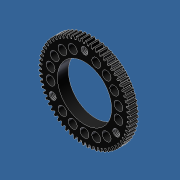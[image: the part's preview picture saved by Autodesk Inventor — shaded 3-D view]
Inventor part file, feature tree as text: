
AUTODESK INVENTOR PART (.ipt)
format: ipt  version: unknown  size: 705,536 bytes
history: native  units: in
note: dims shown in document units (in); Inventor stores cm internally (conversion verified against a paired STEP export)
features: sketch x5, extrude x4, hole x1
ambient origin geometry x8: Origin, YZ Plane, XZ Plane, XY Plane, X Axis, Y Axis, Z Axis, Center Point
bodies: Solid1 (feature_tree)
feature tree (10):
  extrude  "Extrusion1"  Depth=1.2205in
  extrude  "Extrusion2"  Depth=1.6535in
  hole  "Hole1"  [1 undecoded]
  extrude  "Extrusion3"  Depth=0.2in
  extrude  "Extrusion4"  Depth=0.775in
  sketch  "Sketch1"  dims[d0=0.185in d1=0.0in d2=1.2205in]
  sketch  "Sketch2"  dims[d3=0.185in d4=0.0in d5=1.6535in]
  sketch  "Sketch3"  dims[d6=1.1811in d8=360.0deg]
  sketch  "Sketch4"  dims[d10=0.156in d11=0.75in d12=0.375in d13=0.25in d14=0.5635in d15=1.0in d16=0.8108in d17=1.875in]
  sketch  "Sketch5"  dims[d18=0.0625in d19=0.0in d20=0.2in d21=0.775in d22=7.0866in d24=360.0deg d26=1.0in d27=0.0in]
note: 1 required parameter value undecoded (feature->parameter linkage not recoverable at this tier; creation-order binding heuristic only, values carry confidence <= 0.55)
